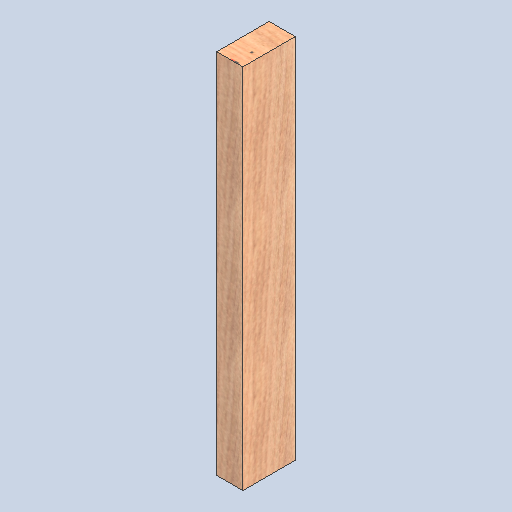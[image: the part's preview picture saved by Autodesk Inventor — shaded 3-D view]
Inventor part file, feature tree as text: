
AUTODESK INVENTOR PART (.ipt)
format: ipt  version: 2025 (Build 290162000, 162)  size: 169,984 bytes
history: native  units: in
note: dims shown in document units (in); Inventor stores cm internally (conversion verified against a paired STEP export)
features: other x3, sketch x1
ambient origin geometry x8: Origin, YZ Plane, XZ Plane, XY Plane, X Axis, Y Axis, Z Axis, Center Point
bodies: Solid1 (feature_tree)
feature tree (4):
  other  "2x4x28.ipt"
  other  "Solid1::2x4x28.ipt"
  other  "TaggingFeature1"
  sketch  "Sketch1"  dims[d0=0.3937in]
